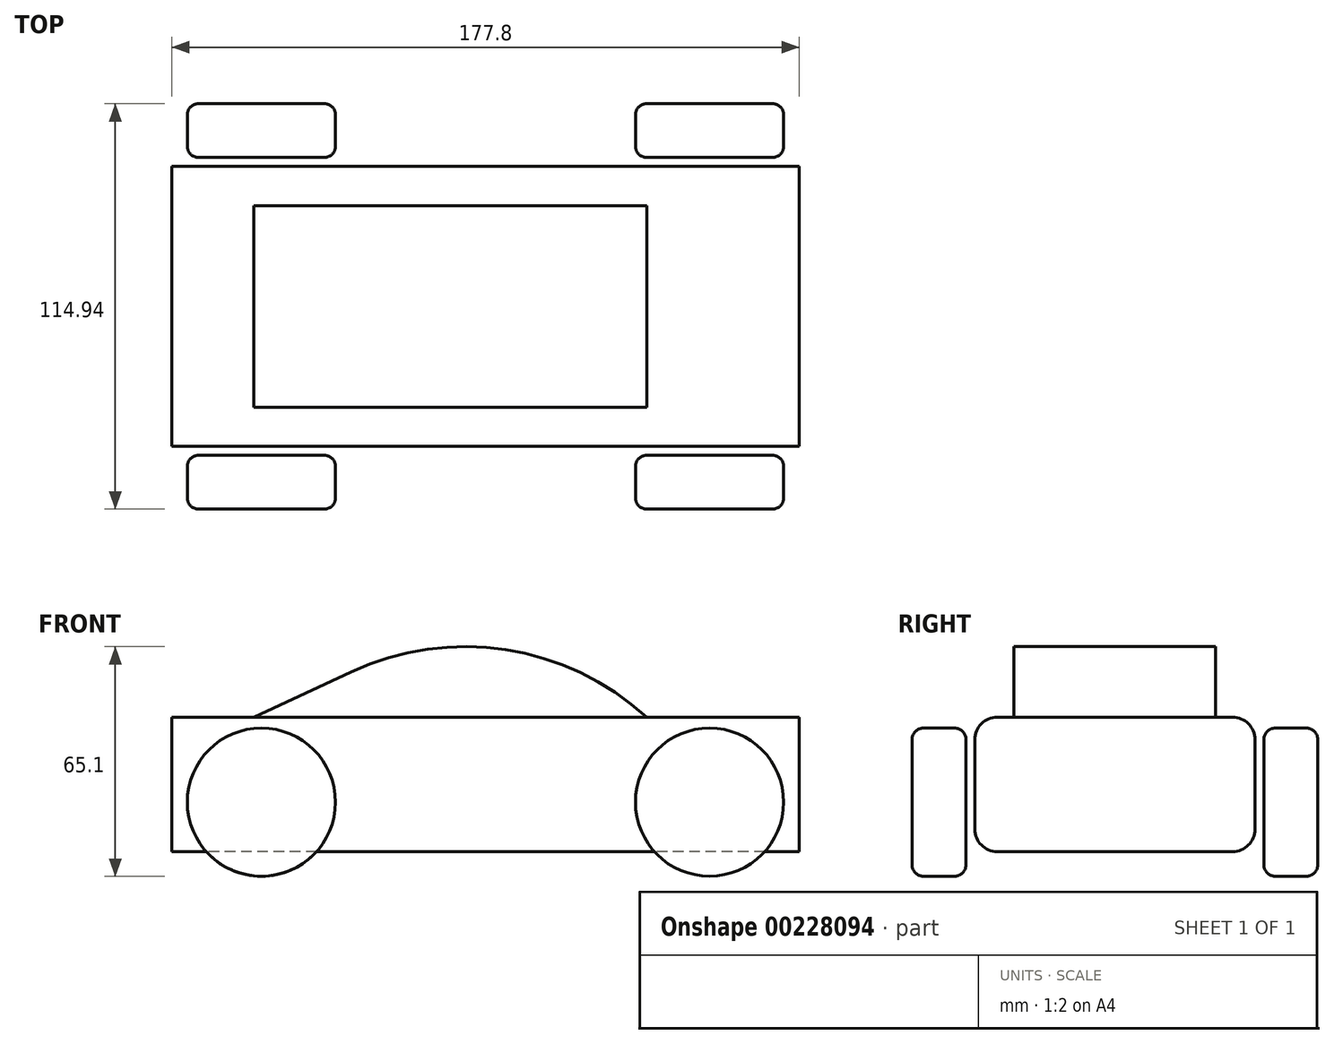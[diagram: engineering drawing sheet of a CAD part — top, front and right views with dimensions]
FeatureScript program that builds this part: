
annotation { "Feature Type Name" : "Feature", "Feature Type Description" : "" }
export const myFeature = defineFeature(function(context is Context, id is Id, definition is map)
    precondition{}
    {
        {
            var Q0;
            Q0=qCreatedBy(makeId("Front.planeOp"),FACE);
            var sketch = newSketch(context, id + "F0", { "sketchPlane" : qUnion([Q0])});
            skLineSegment(sketch, "E0.bottom", {"start": v(88.9, 19.05) * mm, "end": v(-88.9, 19.05) * mm});
            skLineSegment(sketch, "E0.top", {"start": v(88.9, -19.05) * mm, "end": v(-88.9, -19.05) * mm});
            skLineSegment(sketch, "E0.left", {"start": v(88.9, 19.05) * mm, "end": v(88.9, -19.05) * mm});
            skLineSegment(sketch, "E0.right", {"start": v(-88.9, 19.05) * mm, "end": v(-88.9, -19.05) * mm});
            skPoint(sketch, "E0.middle", {"position": v(0, 0) * mm});
            skLineSegment(sketch, "E1", {"start": v(-88.9, -26.04) * mm, "end": v(88.9, -26.04) * mm, "construction": true});
            skCircle(sketch, "E2", {"center": v(63.5, -5.04) * mm, "radius": 21 * mm});
            skPoint(sketch, "E3.orphan", {"position": v(34.25, -26.04) * mm});
            skSolve(sketch);
        }
        {
            var Q0;
            Q0=qCreatedBy(makeId("Front.planeOp"),FACE);
            var sketch = newSketch(context, id + "F1", { "sketchPlane" : qUnion([Q0])});
            skLineSegment(sketch, "E4.0", {"start": v(88.9, 19.05) * mm, "end": v(-88.9, 19.05) * mm});
            skLineSegment(sketch, "E5.0", {"start": v(-88.9, 19.05) * mm, "end": v(-88.9, -19.05) * mm});
            skLineSegment(sketch, "E6.0", {"start": v(88.9, -19.05) * mm, "end": v(-88.9, -19.05) * mm});
            skLineSegment(sketch, "E7.0", {"start": v(88.9, 19.05) * mm, "end": v(88.9, -19.05) * mm});
            skSolve(sketch);
        }
        {
            var Q0;
            Q0 = qSketchRegion(id + "F1", true);
            extrude(context, id + "F2", {"entities" : qUnion([Q0]), "endBound" : BoundingType.SYMMETRIC, "depth" : 79.38 * mm});
        }
        {
            var Q0;
            Q0=makeQuery(id+"F2.opExtrude","CAP_FACE",FACE,{"disambiguationData":[OSD([sQuery(id+"F1.wireOp",EDGE,"E4.0"),sQuery(id+"F1.wireOp",EDGE,"E5.0"),sQuery(id+"F1.wireOp",EDGE,"E6.0"),sQuery(id+"F1.wireOp",EDGE,"E7.0")])],"isStart":false});
            cPlane(context, id + "F3", {"entities" : qUnion([Q0]), "cplaneType" : CPlaneType.OFFSET, "offset" : 2.54 * mm, "width" : 152.4 * mm, "height" : 152.4 * mm});
        }
        {
            var Q0;
            Q0=qCreatedBy(id+"F3.planeOp",FACE);
            var sketch = newSketch(context, id + "F4", { "sketchPlane" : qUnion([Q0])});
            skCircle(sketch, "E8.0", {"center": v(63.5, -5.04) * mm, "radius": 21 * mm});
            skSolve(sketch);
        }
        {
            var Q0;
            Q0 = qSketchRegion(id + "F4", true);
            extrude(context, id + "F5", {"entities" : qUnion([Q0]), "depth" : 15.24 * mm});
        }
        {
            var Q0;
            Q0=makeQuery(id+"F2.opExtrude","CAP_EDGE",EDGE,{"disambiguationData":[OSD([sQuery(id+"F1.wireOp",EDGE,"E4.0")])],"isStart":false});
            var Q1;
            Q1=makeQuery(id+"F2.opExtrude","CAP_EDGE",EDGE,{"disambiguationData":[OSD([sQuery(id+"F1.wireOp",EDGE,"E4.0")])],"isStart":true});
            var Q2;
            Q2=makeQuery(id+"F2.opExtrude","CAP_EDGE",EDGE,{"disambiguationData":[OSD([sQuery(id+"F1.wireOp",EDGE,"E6.0")])],"isStart":false});
            var Q3;
            Q3=makeQuery(id+"F2.opExtrude","CAP_EDGE",EDGE,{"disambiguationData":[OSD([sQuery(id+"F1.wireOp",EDGE,"E6.0")])],"isStart":true});
            fillet(context, id + "F6", {"entities" : qUnion([Q0, Q1, Q2, Q3]), "radius" : 6.35 * mm, "tangentPropagation" : true, "allowEdgeOverflow" : false});
        }
        {
            var Q0;
            Q0=makeQuery(id+"F5.opExtrude","CAP_EDGE",EDGE,{"disambiguationData":[OSD([sQuery(id+"F4.wireOp",EDGE,"E8.0")])],"isStart":false});
            var Q1;
            Q1=makeQuery(id+"F5.opExtrude","CAP_EDGE",EDGE,{"disambiguationData":[OSD([sQuery(id+"F4.wireOp",EDGE,"E8.0")])],"isStart":true});
            fillet(context, id + "F7", {"entities" : qUnion([Q0, Q1]), "radius" : 3.17 * mm, "tangentPropagation" : true, "allowEdgeOverflow" : false});
        }
        {
            var Q0;
            Q0=makeQuery(id+"F5.opExtrude","SWEPT_BODY",BODY,{"disambiguationData":[OSD([sQuery(id+"F4.wireOp",EDGE,"E8.0")])]});
            var Q1;
            Q1=qCreatedBy(makeId("Right.planeOp"),FACE);
            mirror(context, id + "F8", {"entities" : qUnion([Q0]), "mirrorPlane" : qUnion([Q1])});
        }
        {
            var Q0;
            Q0=makeQuery(id+"F8.opPattern","COPY",BODY,{"derivedFrom":makeQuery(id+"F5.opExtrude","SWEPT_BODY",BODY,{"disambiguationData":[OSD([sQuery(id+"F4.wireOp",EDGE,"E8.0")])]}),"instanceName":"1"});
            var Q1;
            Q1=makeQuery(id+"F5.opExtrude","SWEPT_BODY",BODY,{"disambiguationData":[OSD([sQuery(id+"F4.wireOp",EDGE,"E8.0")])]});
            var Q2;
            Q2=qCreatedBy(makeId("Front.planeOp"),FACE);
            mirror(context, id + "F9", {"entities" : qUnion([Q0, Q1]), "mirrorPlane" : qUnion([Q2])});
        }
        {
            var Q0;
            Q0=qCreatedBy(makeId("Front.planeOp"),FACE);
            var sketch = newSketch(context, id + "F10", { "sketchPlane" : qUnion([Q0])});
            skLineSegment(sketch, "E9.0", {"start": v(88.9, 19.05) * mm, "end": v(-88.9, 19.05) * mm});
            skLineSegment(sketch, "E10.0", {"start": v(88.9, 12.7) * mm, "end": v(-88.9, 12.7) * mm});
            skLineSegment(sketch, "E11", {"start": v(-65.66, 19.05) * mm, "end": v(-38.1, 31.9) * mm});
            skArc(sketch, "E12", {"start": v(-38.1, 31.9) * mm, "mid": v(5.76, 38.18) * mm, "end": v(45.72, 19.05) * mm});
            skSolve(sketch);
        }
        {
            var Q0;
            Q0 = qSketchRegion(id + "F10", true);
            extrude(context, id + "F11", {"entities" : qUnion([Q0]), "operationType" : NewBodyOperationType.ADD, "endBound" : BoundingType.SYMMETRIC, "depth" : 57.15 * mm});
        }
    });
